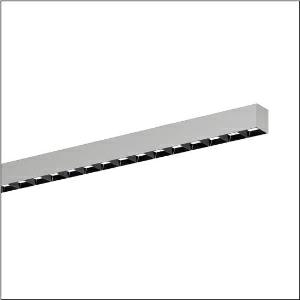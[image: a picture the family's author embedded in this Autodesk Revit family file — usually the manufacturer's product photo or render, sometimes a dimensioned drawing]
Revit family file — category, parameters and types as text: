
# Revit family: silica_r__21_51mx21dc3asb_b009
name_source: partatom
category: Lighting Fixtures
units: mm (PartAtom-declared; Revit-internal decimal feet)

## family parameters
Cut with Voids When Loaded = No
Host = Face
Light Source = No
Part Type = Normal
Room Calculation Point = No
Round Connector Dimension = Use Diameter
Shared = No

## types (1)
- --- (1 x LED, 10800 lm, 69.3 W, 3000K)
    Apparent Load = 69 VA
    CIE Flux Codes = 87 99 100 100 100
    Color Rendering = 80
    Color Temperature = 3000K
    Default Elevation = 1800 mm
    Description = Silica® 21, office luminaire, primary light control with darklight reflector, of PMMA, black, CAT 2 (L<= 3000cd/m²), light emission: direct distribution, primary light characteristic: symmetric, installation type: surface-mounted, LED, rated luminous flux: 10.800lm, luminous efficacy: 156lm/W, light colour: 830, colour temperature: 3000K, with terminal, 3+2-pole, max. 2.5mm², mains connection: 220..240V, AC, 50/60Hz, luminaire housing, of aluminium, metallic grey (RAL 9006), length: 3.004mm, width: 53mm, height: 53mm, protection rating (complete): IP20, insulation class (complete): insulation class I (protective earthing), certification: CE, permissible operating ambient temperature: 0..+35°C, standard: EN 50419, packaging unit: 1 piece
    Height = 0 mm  [stored 0 ft]
    Lamp = 1 x LED
    Lamp Light Flux = 10800 lm
    Lamp Power = 69.3 W
    Lamp count = 1
    Length = 3004 mm
    Luminous efficacy = 156 lm/W
    Manufacturer = Siteco
    ModVariant = No
    Model = 51MX21DC3ASB
    Mounting Place = Ceiling
    Mounting Type = Recessed
    Number of Poles = 1
    OnlyDefault = Yes
    Power Factor = 1
    Product Name = Silica® 21
    Product group = office luminaire | ceiling recessed
    ProductGroupID = 401
    Protection Class = Protection class I
    Protection Degree = IP 20
    RLX_Detail_Level = 1
    RLX_Emergency_Light_Flux = 0 lm
    RLX_Emergency_Type = 0
    RLX_Emergency_Type_DB = No
    RlxData = <blob elided: 63229 chars, md5=c4ba3dfb>
    Socket = socket
    Standby Power = 0 W
    System Light Flux = 10800 lm
    System Power = 69 W
    Type Comments = factory setting: luminous flux: 100 % | dim-lin: 254 | 393 mA
    Type Image = l_1313585.jpg
    URL = http://relux.com
    VarID = @adj_072433
    Voltage = 0 V
    Weight = 0.00 kg
    Width = 53 mm

note: [stored X ft] marks values corroborated as IEEE doubles in the binary element streams (Revit-internal decimal feet)

## geometry (parser evidence)
native form markers: Blend x4, Sweep x11
no freeform markers — native parametric forms only
